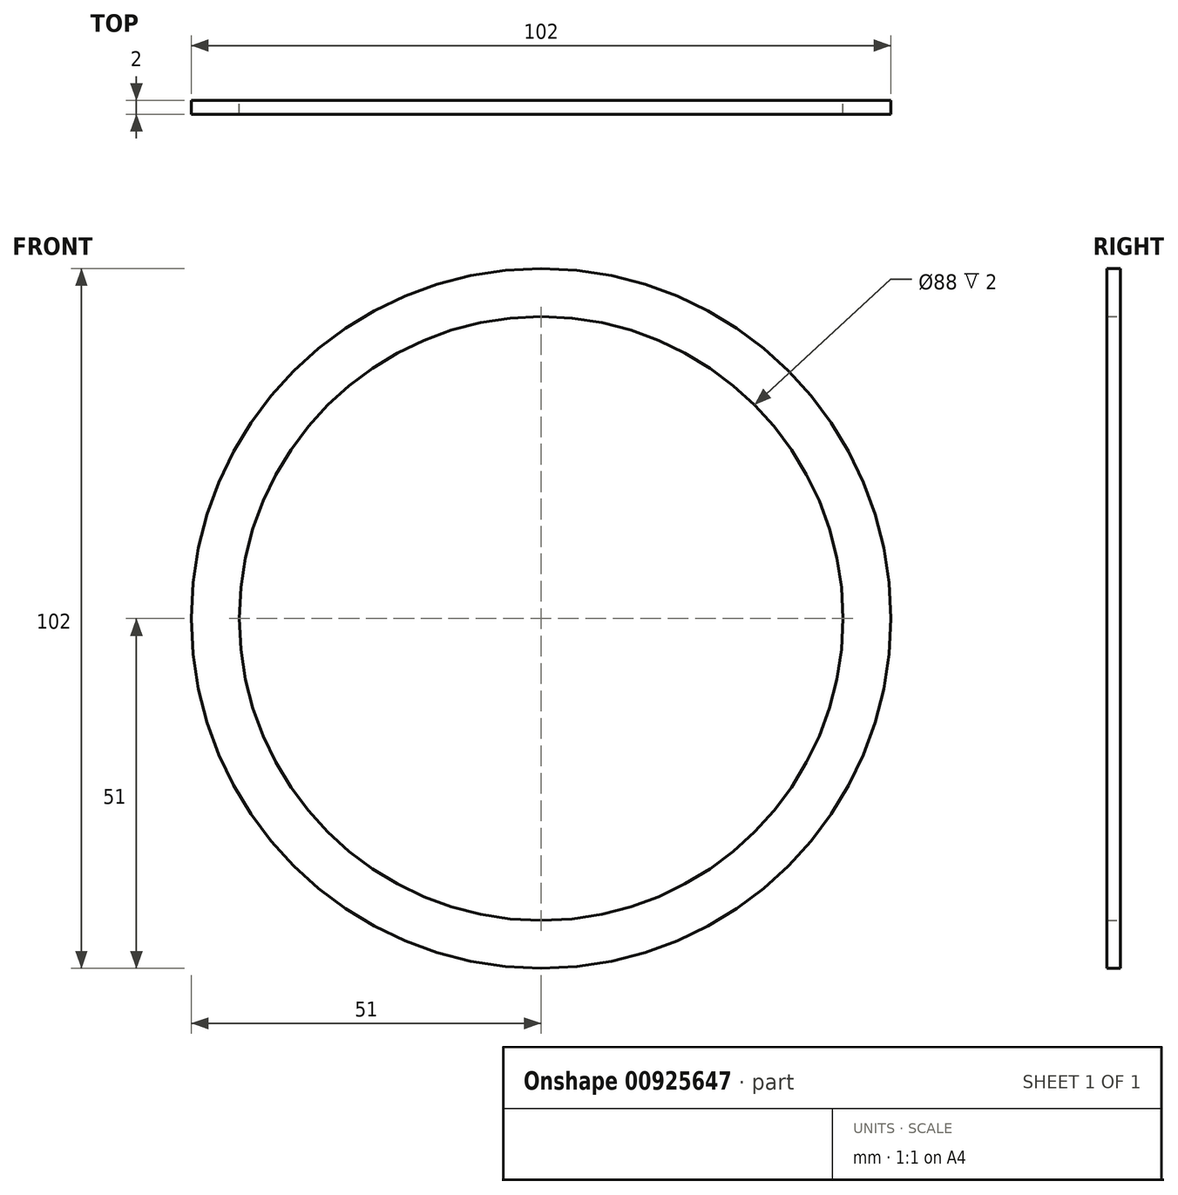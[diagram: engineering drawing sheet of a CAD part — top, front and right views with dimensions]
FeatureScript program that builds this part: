
annotation { "Feature Type Name" : "Feature", "Feature Type Description" : "" }
export const myFeature = defineFeature(function(context is Context, id is Id, definition is map)
    precondition{}
    {
        {
            var Q0;
            Q0=qCreatedBy(makeId("Front.planeOp"),FACE);
            var sketch = newSketch(context, id + "F0", { "sketchPlane" : qUnion([Q0])});
            skCircle(sketch, "E0", {"center": v(0, 0) * mm, "radius": 51 * mm});
            skCircle(sketch, "E1", {"center": v(0, 0) * mm, "radius": 44 * mm});
            skSolve(sketch);
        }
        {
            var Q0;
            Q0=makeQuery(id+"F0.imprint","IMPRINT",FACE,{"disambiguationData":[TD([[makeQuery(id+"F0.imprint","IMPRINT",EDGE,{"derivedFrom":sQuery(id+"F0.wireOp",EDGE,"E0")}),1.0]])]});
            extrude(context, id + "F1", {"entities" : qUnion([Q0]), "depth" : 2 * mm, "offsetDistance" : 25 * mm});
        }
    });
